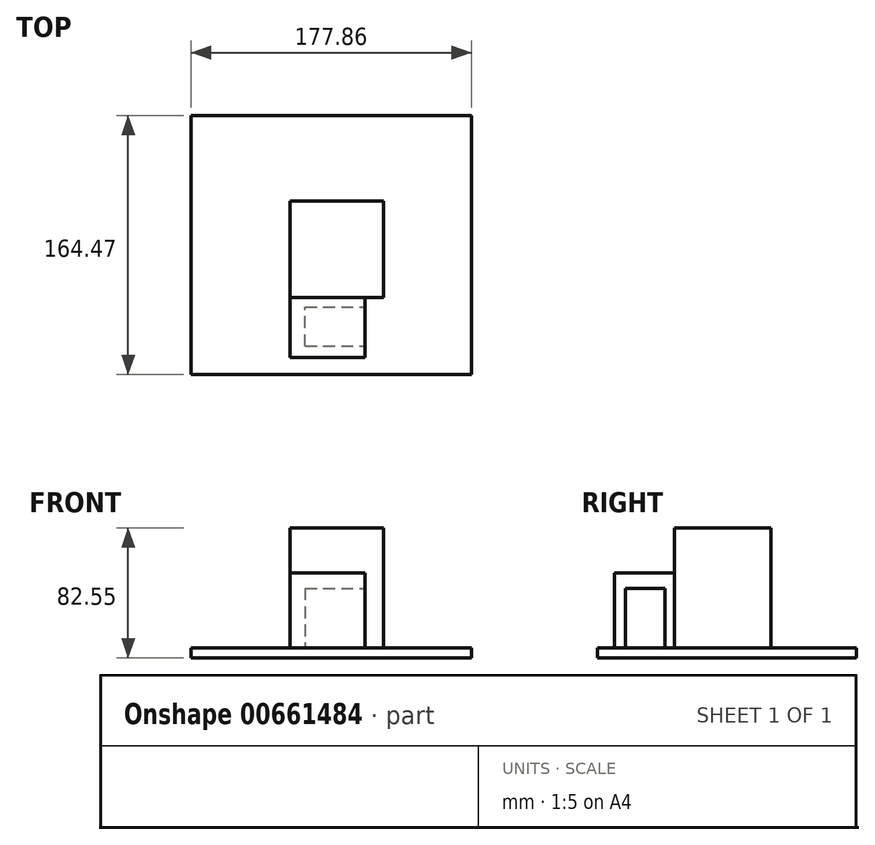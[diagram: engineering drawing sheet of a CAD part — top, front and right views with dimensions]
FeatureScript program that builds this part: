
annotation { "Feature Type Name" : "Feature", "Feature Type Description" : "" }
export const myFeature = defineFeature(function(context is Context, id is Id, definition is map)
    precondition{}
    {
        {
            var Q0;
            Q0=qCreatedBy(makeId("Top.planeOp"),FACE);
            var sketch = newSketch(context, id + "F0", { "sketchPlane" : qUnion([Q0])});
            skLineSegment(sketch, "E0.bottom", {"start": v(-89.48, 80.91) * mm, "end": v(88.38, 80.91) * mm});
            skLineSegment(sketch, "E0.top", {"start": v(-89.48, -83.56) * mm, "end": v(88.38, -83.56) * mm});
            skLineSegment(sketch, "E0.left", {"start": v(-89.48, 80.91) * mm, "end": v(-89.48, -83.56) * mm});
            skLineSegment(sketch, "E0.right", {"start": v(88.38, 80.91) * mm, "end": v(88.38, -83.56) * mm});
            skSolve(sketch);
        }
        {
            var Q0;
            Q0=makeQuery(id+"F0.imprint","IMPRINT",FACE,{"disambiguationData":[TD([[makeQuery(id+"F0.imprint","IMPRINT",EDGE,{"derivedFrom":sQuery(id+"F0.wireOp",EDGE,"E0.bottom")}),-1.0]])]});
            extrude(context, id + "F1", {"entities" : qUnion([Q0]), "depth" : 6.35 * mm, "offsetDistance" : 25.4 * mm});
        }
        {
            var Q0;
            Q0=makeQuery(id+"F1.opExtrude","CAP_FACE",FACE,{"disambiguationData":[OSD([sQuery(id+"F0.wireOp",EDGE,"E0.bottom"),sQuery(id+"F0.wireOp",EDGE,"E0.top"),sQuery(id+"F0.wireOp",EDGE,"E0.left"),sQuery(id+"F0.wireOp",EDGE,"E0.right")])],"isStart":false});
            var sketch = newSketch(context, id + "F2", { "sketchPlane" : qUnion([Q0])});
            skLineSegment(sketch, "E1.bottom", {"start": v(-26.65, -34.57) * mm, "end": v(32.65, -34.57) * mm});
            skLineSegment(sketch, "E1.top", {"start": v(-26.65, 26.66) * mm, "end": v(32.65, 26.66) * mm});
            skLineSegment(sketch, "E1.left", {"start": v(-26.65, -34.57) * mm, "end": v(-26.65, 26.66) * mm});
            skLineSegment(sketch, "E1.right", {"start": v(32.65, -34.57) * mm, "end": v(32.65, 26.66) * mm});
            skSolve(sketch);
        }
        {
            var Q0;
            Q0 = qSketchRegion(id + "F2", true);
            extrude(context, id + "F3", {"entities" : qUnion([Q0]), "operationType" : NewBodyOperationType.ADD, "depth" : 76.2 * mm, "offsetDistance" : 25.4 * mm});
        }
        {
            var Q0;
            Q0=makeQuery(id+"F3.opExtrude","SWEPT_FACE",FACE,{"disambiguationData":[OSD([sQuery(id+"F2.wireOp",EDGE,"E1.bottom")])]});
            var sketch = newSketch(context, id + "F4", { "sketchPlane" : qUnion([Q0])});
            skLineSegment(sketch, "E2.bottom", {"start": v(20.96, 54.05) * mm, "end": v(-26.65, 54.05) * mm});
            skLineSegment(sketch, "E2.top", {"start": v(20.96, 6.35) * mm, "end": v(-26.65, 6.35) * mm});
            skLineSegment(sketch, "E2.left", {"start": v(20.96, 54.05) * mm, "end": v(20.96, 6.35) * mm});
            skLineSegment(sketch, "E2.right", {"start": v(-26.65, 54.05) * mm, "end": v(-26.65, 6.35) * mm});
            skSolve(sketch);
        }
        {
            var Q0;
            Q0 = qSketchRegion(id + "F4", true);
            extrude(context, id + "F5", {"entities" : qUnion([Q0]), "operationType" : NewBodyOperationType.ADD, "depth" : 38.1 * mm, "offsetDistance" : 25.4 * mm});
        }
        {
            var Q0;
            Q0=makeQuery(id+"F5.opExtrude","SWEPT_FACE",FACE,{"disambiguationData":[OSD([sQuery(id+"F4.wireOp",EDGE,"E2.left")])]});
            var sketch = newSketch(context, id + "F6", { "sketchPlane" : qUnion([Q0])});
            skLineSegment(sketch, "E3.bottom", {"start": v(-65.5, 44.2) * mm, "end": v(-40.56, 44.2) * mm});
            skLineSegment(sketch, "E3.top", {"start": v(-65.5, 6.35) * mm, "end": v(-40.56, 6.35) * mm});
            skLineSegment(sketch, "E3.left", {"start": v(-65.5, 44.2) * mm, "end": v(-65.5, 6.35) * mm});
            skLineSegment(sketch, "E3.right", {"start": v(-40.56, 44.2) * mm, "end": v(-40.56, 6.35) * mm});
            skSolve(sketch);
        }
        {
            var Q0;
            Q0=makeQuery(id+"F6.imprint","IMPRINT",FACE,{"disambiguationData":[TD([[makeQuery(id+"F6.imprint","IMPRINT",EDGE,{"derivedFrom":sQuery(id+"F6.wireOp",EDGE,"E3.bottom")}),-1.0]])]});
            extrude(context, id + "F7", {"entities" : qUnion([Q0]), "operationType" : NewBodyOperationType.REMOVE, "oppositeDirection" : true, "depth" : 38.1 * mm, "offsetDistance" : 25.4 * mm});
        }
    });
